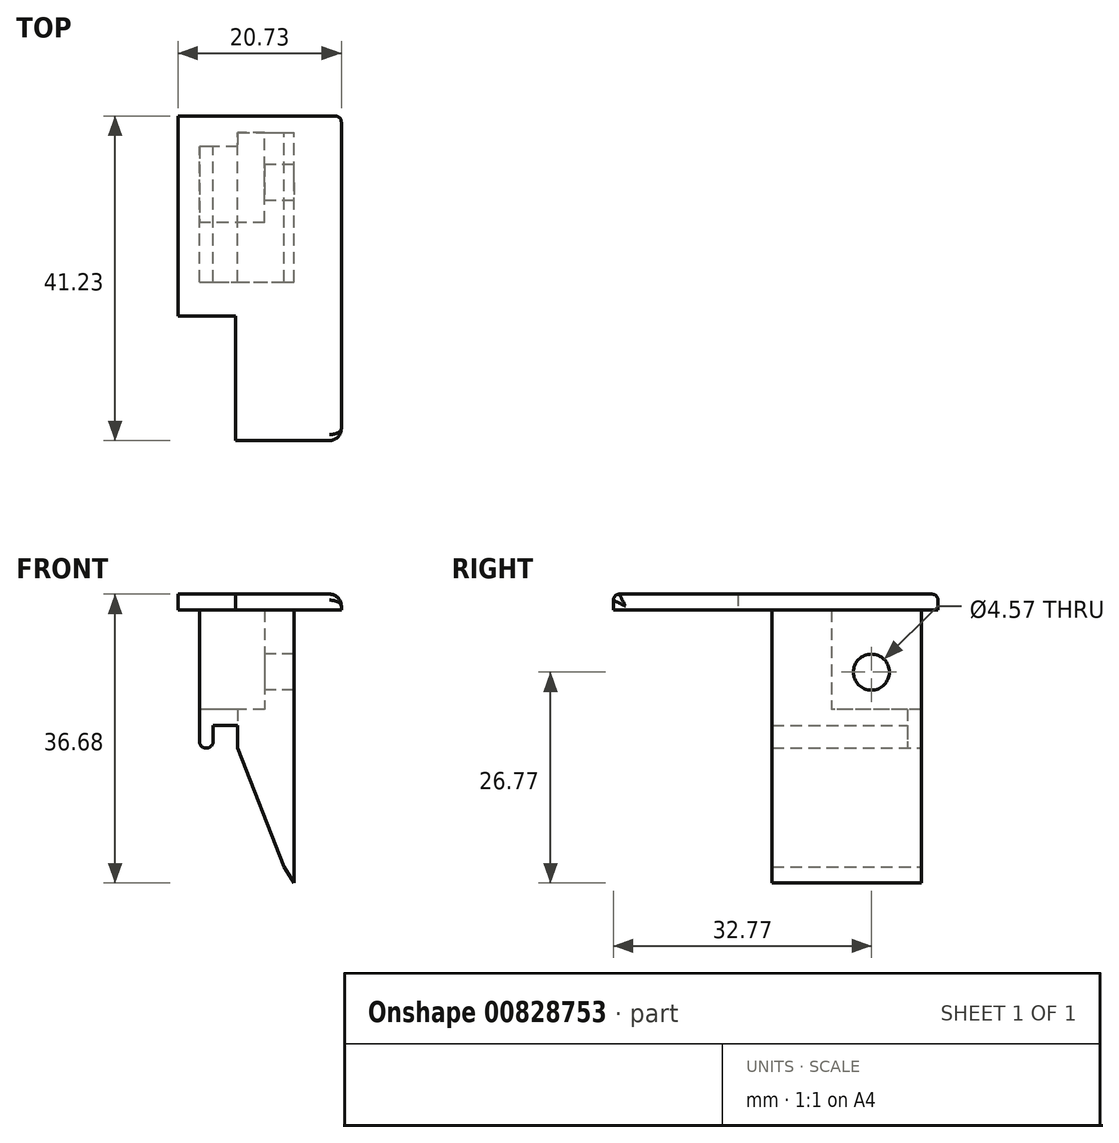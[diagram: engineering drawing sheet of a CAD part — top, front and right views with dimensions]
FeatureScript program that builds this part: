
annotation { "Feature Type Name" : "Feature", "Feature Type Description" : "" }
export const myFeature = defineFeature(function(context is Context, id is Id, definition is map)
    precondition{}
    {
        {
            var Q0;
            Q0=qCreatedBy(makeId("Front.planeOp"),FACE);
            var sketch = newSketch(context, id + "F0", { "sketchPlane" : qUnion([Q0])});
            skLineSegment(sketch, "E0", {"start": v(-12.01, 26.3) * mm, "end": v(-12.01, 8.78) * mm});
            skLineSegment(sketch, "E1", {"start": v(-12.01, 8.78) * mm, "end": v(-10.26, 8.78) * mm});
            skLineSegment(sketch, "E2", {"start": v(-10.26, 8.78) * mm, "end": v(-10.26, 11.67) * mm});
            skLineSegment(sketch, "E3", {"start": v(-10.26, 11.67) * mm, "end": v(-7.14, 11.67) * mm});
            skLineSegment(sketch, "E4", {"start": v(-7.14, 11.67) * mm, "end": v(-7.14, 8.78) * mm});
            skLineSegment(sketch, "E5", {"start": v(-12.01, 26.3) * mm, "end": v(0, 26.3) * mm});
            skLineSegment(sketch, "E6", {"start": v(0, 26.3) * mm, "end": v(0, -8.34) * mm});
            skLineSegment(sketch, "E7", {"start": v(-7.14, 8.78) * mm, "end": v(-1.25, -6.3) * mm});
            skLineSegment(sketch, "E8", {"start": v(-1.25, -6.3) * mm, "end": v(0, -8.34) * mm});
            skSolve(sketch);
        }
        {
            var Q0;
            Q0=makeQuery(id+"F0.imprint","IMPRINT",FACE,{"disambiguationData":[TD([[makeQuery(id+"F0.imprint","IMPRINT",EDGE,{"derivedFrom":sQuery(id+"F0.wireOp",EDGE,"E0")}),1.0]])]});
            extrude(context, id + "F1", {"entities" : qUnion([Q0]), "depth" : 18.95 * mm, "offsetDistance" : 25.4 * mm});
        }
        {
            var Q0;
            Q0=makeQuery(id+"F1.opExtrude","SWEPT_FACE",FACE,{"disambiguationData":[OSD([sQuery(id+"F0.wireOp",EDGE,"E5")])]});
            var sketch = newSketch(context, id + "F2", { "sketchPlane" : qUnion([Q0])});
            skLineSegment(sketch, "E9", {"start": v(-14.7, 2.1) * mm, "end": v(6.02, 2.1) * mm});
            skLineSegment(sketch, "E10", {"start": v(6.02, 2.1) * mm, "end": v(6.02, -39.12) * mm});
            skLineSegment(sketch, "E11", {"start": v(6.02, -39.12) * mm, "end": v(-7.41, -39.12) * mm});
            skLineSegment(sketch, "E12", {"start": v(-7.41, -39.12) * mm, "end": v(-7.41, -23.3) * mm});
            skLineSegment(sketch, "E13", {"start": v(-7.41, -23.3) * mm, "end": v(-14.7, -23.3) * mm});
            skLineSegment(sketch, "E14", {"start": v(-14.7, -23.3) * mm, "end": v(-14.7, 2.1) * mm});
            skSolve(sketch);
        }
        {
            var Q0;
            Q0=qSketchRegion(id+"F2",true);
            extrude(context, id + "F3", {"entities" : qUnion([Q0]), "operationType" : NewBodyOperationType.ADD, "depth" : 2.03 * mm, "offsetDistance" : 25.4 * mm});
        }
        {
            var Q0;
            Q0=makeQuery(id+"F1.opExtrude","SWEPT_EDGE",EDGE,{"disambiguationData":[OSD([sQuery(id+"F0.wireOp",EDGE,"E0"),sQuery(id+"F0.wireOp",EDGE,"E1")])]});
            var Q1;
            Q1=makeQuery(id+"F1.opExtrude","SWEPT_EDGE",EDGE,{"disambiguationData":[OSD([sQuery(id+"F0.wireOp",EDGE,"E1"),sQuery(id+"F0.wireOp",EDGE,"E2")])]});
            fillet(context, id + "F4", {"entities" : qUnion([Q0, Q1]), "radius" : 0.84 * mm, "tangentPropagation" : true, "allowEdgeOverflow" : false});
        }
        {
            var Q0;
            Q0=makeQuery(id+"F1.opExtrude","SWEPT_FACE",FACE,{"disambiguationData":[OSD([sQuery(id+"F0.wireOp",EDGE,"E0")])]});
            var sketch = newSketch(context, id + "F5", { "sketchPlane" : qUnion([Q0])});
            skLineSegment(sketch, "E15.bottom", {"start": v(0, 26.3) * mm, "end": v(11.43, 26.3) * mm});
            skLineSegment(sketch, "E15.top", {"start": v(0, 13.7) * mm, "end": v(11.43, 13.7) * mm});
            skLineSegment(sketch, "E15.left", {"start": v(0, 26.3) * mm, "end": v(0, 13.7) * mm});
            skLineSegment(sketch, "E15.right", {"start": v(11.43, 26.3) * mm, "end": v(11.43, 13.7) * mm});
            skPoint(sketch, "E16", {"position": v(6.17, 18.35) * mm});
            skSolve(sketch);
        }
        {
            var Q0;
            Q0=qSketchRegion(id+"F5",true);
            extrude(context, id + "F6", {"entities" : qUnion([Q0]), "operationType" : NewBodyOperationType.REMOVE, "oppositeDirection" : true, "depth" : 8.3 * mm, "offsetDistance" : 25.4 * mm});
        }
        {
            var Q0;
            Q0=makeQuery(id+"F6.boolean.opBoolean","COPY",FACE,{"derivedFrom":makeQuery(id+"F6.opExtrude","CAP_FACE",FACE,{"disambiguationData":[OSD([sQuery(id+"F5.wireOp",EDGE,"E15.bottom"),sQuery(id+"F5.wireOp",EDGE,"E15.top"),sQuery(id+"F5.wireOp",EDGE,"E15.left"),sQuery(id+"F5.wireOp",EDGE,"E15.right")])],"isStart":false})});
            var sketch = newSketch(context, id + "F7", { "sketchPlane" : qUnion([Q0])});
            skLineSegment(sketch, "E17.bottom", {"start": v(0, 26.3) * mm, "end": v(11.43, 26.3) * mm});
            skLineSegment(sketch, "E17.top", {"start": v(0, 13.7) * mm, "end": v(11.43, 13.7) * mm});
            skLineSegment(sketch, "E17.left", {"start": v(0, 26.3) * mm, "end": v(0, 13.7) * mm});
            skLineSegment(sketch, "E17.right", {"start": v(11.43, 26.3) * mm, "end": v(11.43, 13.7) * mm});
            skPoint(sketch, "E18", {"position": v(6.35, 18.43) * mm});
            skSolve(sketch);
        }
        {
            var Q0;
            Q0=sQuery(id+"F7.wireOp",VERTEX,"E18");
            var Q1;
            Q1=makeQuery(id+"F1.opExtrude","SWEPT_BODY",BODY,{"disambiguationData":[OSD([sQuery(id+"F0.wireOp",EDGE,"E0"),sQuery(id+"F0.wireOp",EDGE,"E1"),sQuery(id+"F0.wireOp",EDGE,"E2"),sQuery(id+"F0.wireOp",EDGE,"E3"),sQuery(id+"F0.wireOp",EDGE,"E4"),sQuery(id+"F0.wireOp",EDGE,"E5"),sQuery(id+"F0.wireOp",EDGE,"E6"),sQuery(id+"F0.wireOp",EDGE,"E7"),sQuery(id+"F0.wireOp",EDGE,"E8")])]});
            hole(context, id + "F8", {"style" : HoleStyle.SIMPLE, "endStyle" : HoleEndStyle.THROUGH, "holeDiameter" : 4.57 * mm, "majorDiameter" : 6.35 * mm, "isTappedThrough" : true, "tappedDepth" : 12.7 * mm, "tapClearance" : 3, "locations" : qUnion([Q0]), "scope" : qUnion([Q1])});
        }
        {
            var Q0;
            Q0=makeQuery(id+"F1.opExtrude","SWEPT_FACE",FACE,{"disambiguationData":[OSD([sQuery(id+"F0.wireOp",EDGE,"E0")])]});
            var sketch = newSketch(context, id + "F9", { "sketchPlane" : qUnion([Q0])});
            skLineSegment(sketch, "E19.bottom", {"start": v(0, 13.7) * mm, "end": v(1.77, 13.7) * mm});
            skLineSegment(sketch, "E19.top", {"start": v(0, 8.5) * mm, "end": v(1.77, 8.5) * mm});
            skLineSegment(sketch, "E19.left", {"start": v(0, 13.7) * mm, "end": v(0, 8.5) * mm});
            skLineSegment(sketch, "E19.right", {"start": v(1.77, 13.7) * mm, "end": v(1.77, 8.5) * mm});
            skSolve(sketch);
        }
        {
            var Q0;
            Q0 = qSketchRegion(id + "F9", true);
            extrude(context, id + "F10", {"entities" : qUnion([Q0]), "operationType" : NewBodyOperationType.REMOVE, "oppositeDirection" : true, "depth" : 4.88 * mm, "offsetDistance" : 25.4 * mm});
        }
        {
            var Q0;
            Q0=makeQuery(id+"F3.opExtrude","CAP_EDGE",EDGE,{"disambiguationData":[OSD([sQuery(id+"F2.wireOp",EDGE,"E11")])],"isStart":false});
            fillet(context, id + "F11", {"entities" : qUnion([Q0]), "radius" : 0.76 * mm, "tangentPropagation" : true, "allowEdgeOverflow" : false});
        }
        {
            var Q0;
            Q0=makeQuery(id+"F3.opExtrude","CAP_EDGE",EDGE,{"disambiguationData":[OSD([sQuery(id+"F2.wireOp",EDGE,"E10")])],"isStart":false});
            fillet(context, id + "F12", {"entities" : qUnion([Q0]), "radius" : 1.52 * mm, "tangentPropagation" : true, "allowEdgeOverflow" : false});
        }
        {
            var Q0;
            Q0=makeQuery(id+"F3.opExtrude","CAP_EDGE",EDGE,{"disambiguationData":[OSD([sQuery(id+"F2.wireOp",EDGE,"E9")])],"isStart":false});
            fillet(context, id + "F13", {"entities" : qUnion([Q0]), "radius" : 0.76 * mm, "tangentPropagation" : true, "allowEdgeOverflow" : false});
        }
    });
